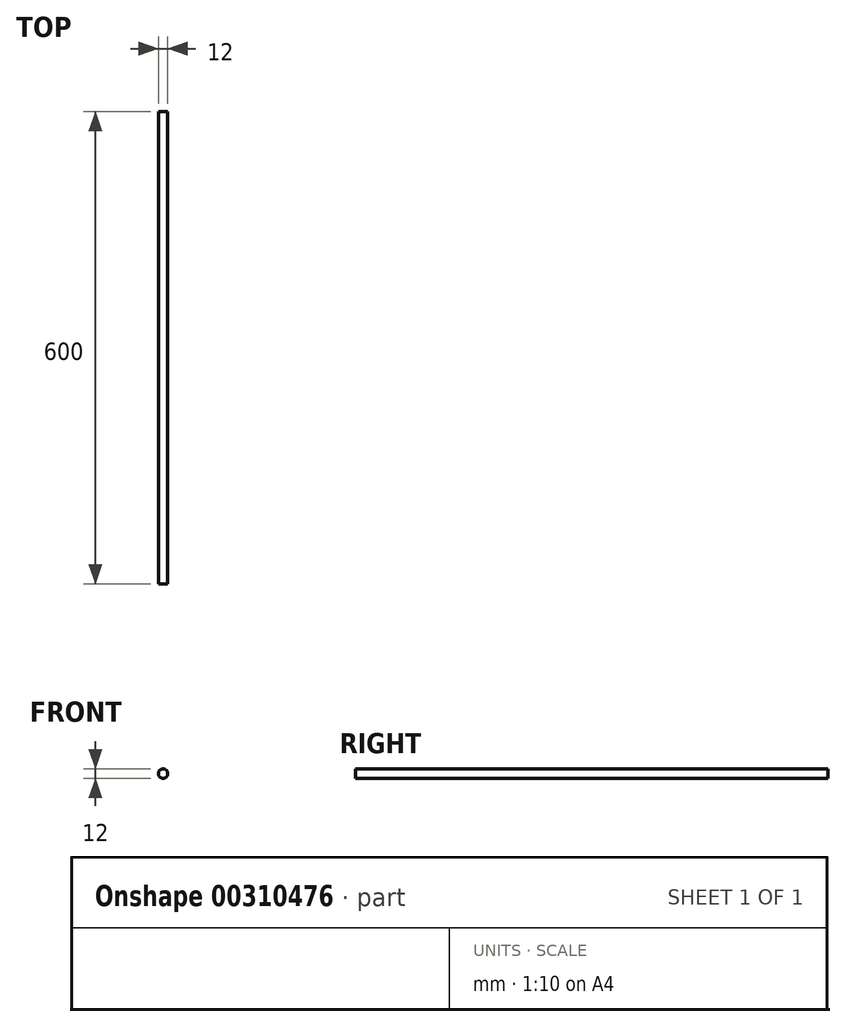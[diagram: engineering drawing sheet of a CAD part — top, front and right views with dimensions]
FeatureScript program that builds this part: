
annotation { "Feature Type Name" : "Feature", "Feature Type Description" : "" }
export const myFeature = defineFeature(function(context is Context, id is Id, definition is map)
    precondition{}
    {
        {
            var Q0;
            Q0=qCreatedBy(makeId("Front.planeOp"),FACE);
            var sketch = newSketch(context, id + "F0", { "sketchPlane" : qUnion([Q0])});
            skCircle(sketch, "E0", {"center": v(0, 0) * mm, "radius": 6 * mm});
            skSolve(sketch);
        }
        {
            var Q0;
            Q0=makeQuery(id+"F0.imprint","IMPRINT",FACE,{"disambiguationData":[TD([[makeQuery(id+"F0.imprint","IMPRINT",EDGE,{"derivedFrom":sQuery(id+"F0.wireOp",EDGE,"E0")}),1.0]])]});
            extrude(context, id + "F1", {"entities" : qUnion([Q0]), "depth" : 600 * mm});
        }
    });
